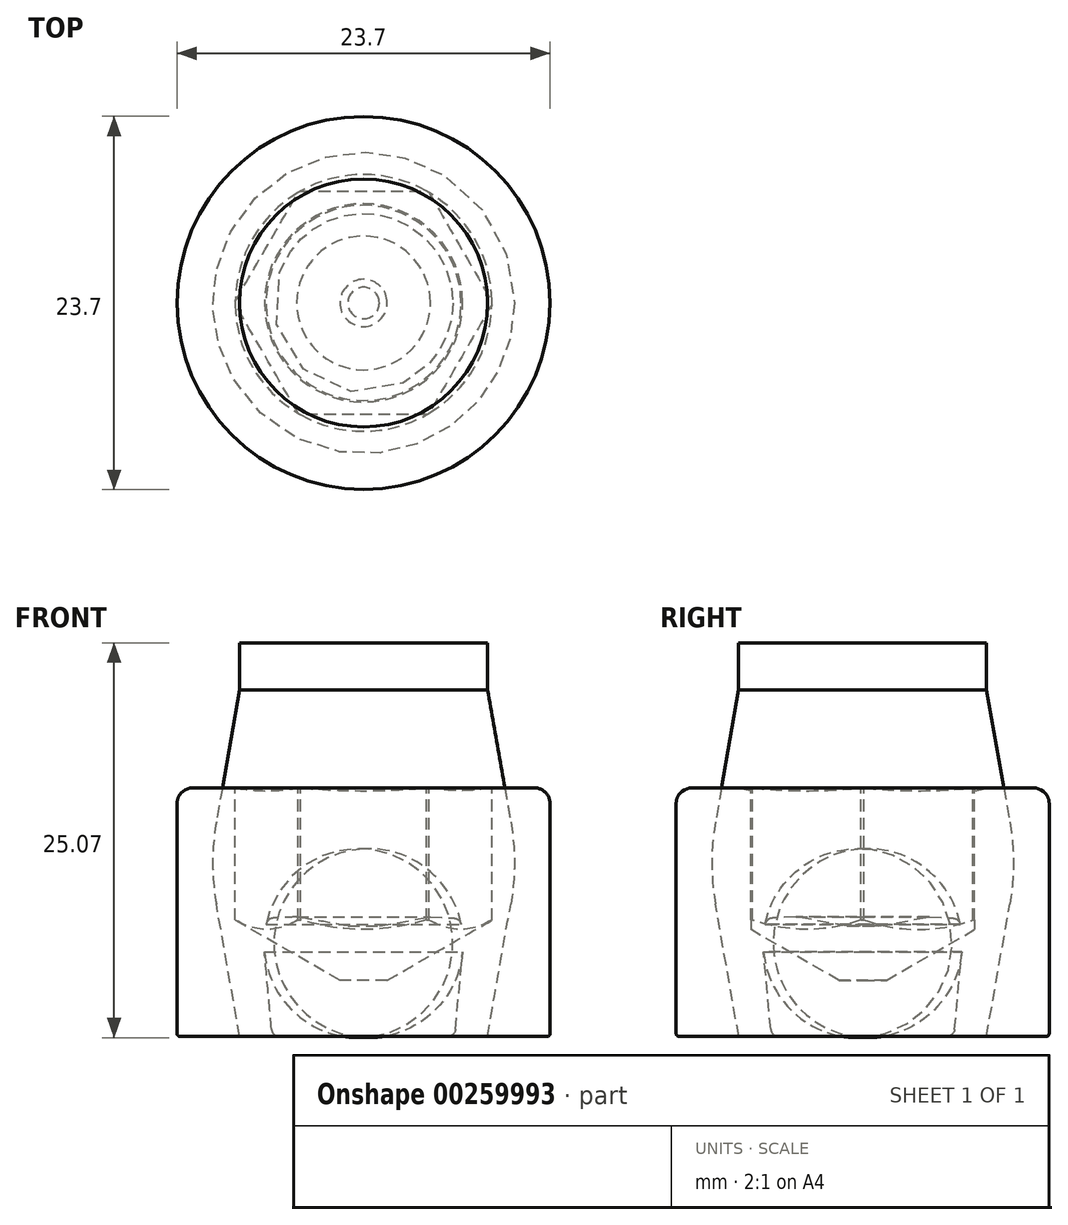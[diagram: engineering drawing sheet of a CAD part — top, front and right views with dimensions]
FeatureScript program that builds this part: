
annotation { "Feature Type Name" : "Feature", "Feature Type Description" : "" }
export const myFeature = defineFeature(function(context is Context, id is Id, definition is map)
    precondition{}
    {
        {
            var Q0;
            Q0=qCreatedBy(makeId("Front.planeOp"),FACE);
            var sketch = newSketch(context, id + "F0", { "sketchPlane" : qUnion([Q0])});
            skLineSegment(sketch, "E0", {"start": v(0, 0) * mm, "end": v(0, 3.56) * mm, "construction": true});
            skLineSegment(sketch, "E1", {"start": v(8.15, 15.8) * mm, "end": v(10.84, 15.8) * mm});
            skLineSegment(sketch, "E2", {"start": v(11.84, 14.8) * mm, "end": v(11.85, 0.2) * mm});
            skLineSegment(sketch, "E3", {"start": v(11.65, 0) * mm, "end": v(0, 0) * mm});
            skPoint(sketch, "E4.visualSharp", {"position": v(11.84, 15.8) * mm});
            skArc(sketch, "E4.filletArc", {"start": v(11.84, 14.8) * mm, "mid": v(11.55, 15.5) * mm, "end": v(10.84, 15.8) * mm});
            skPoint(sketch, "E5.visualSharp", {"position": v(11.85, 0) * mm});
            skArc(sketch, "E5.filletArc", {"start": v(11.65, 0) * mm, "mid": v(11.79, 0.06) * mm, "end": v(11.85, 0.2) * mm});
            skLineSegment(sketch, "E6", {"start": v(8.15, 15.8) * mm, "end": v(8.15, 7.4) * mm});
            skLineSegment(sketch, "E7", {"start": v(8.15, 7.4) * mm, "end": v(1.5, 3.56) * mm});
            skLineSegment(sketch, "E8", {"start": v(1.5, 3.56) * mm, "end": v(0, 3.56) * mm});
            skLineSegment(sketch, "E9", {"start": v(0, 3.56) * mm, "end": v(0, 0) * mm});
            skSolve(sketch);
        }
        {
            var Q0;
            Q0=qSketchRegion(id+"F0",true);
            var Q1;
            Q1=sQuery(id+"F0.wireOp",EDGE,"E9");
            revolve(context, id + "F1", {"entities" : qUnion([Q0]), "axis" : qUnion([Q1]), "revolveType" : RevolveType.FULL});
        }
        {
            var Q0;
            Q0=makeQuery(id+"F1.opRevolve","SWEPT_FACE",FACE,{"disambiguationData":[OSD([sQuery(id+"F0.wireOp",EDGE,"E1")])]});
            var sketch = newSketch(context, id + "F2", { "sketchPlane" : qUnion([Q0])});
            skCircle(sketch, "E10", {"center": v(0, 0) * mm, "radius": 10.84 * mm});
            skCircle(sketch, "E11.cCircle", {"center": v(0, 0) * mm, "radius": 7.1 * mm, "construction": true});
            skLineSegment(sketch, "E11.0", {"start": v(-4.1, 7.1) * mm, "end": v(4.1, 7.1) * mm});
            skLineSegment(sketch, "E11.1", {"start": v(4.1, 7.1) * mm, "end": v(8.2, 0) * mm});
            skLineSegment(sketch, "E11.2", {"start": v(8.2, 0) * mm, "end": v(4.1, -7.1) * mm});
            skLineSegment(sketch, "E11.3", {"start": v(4.1, -7.1) * mm, "end": v(-4.1, -7.1) * mm});
            skLineSegment(sketch, "E11.4", {"start": v(-4.1, -7.1) * mm, "end": v(-8.2, 0) * mm});
            skLineSegment(sketch, "E11.5", {"start": v(-8.2, 0) * mm, "end": v(-4.1, 7.1) * mm});
            skPoint(sketch, "E11.0.midPoint", {"position": v(0, 7.1) * mm});
            skSolve(sketch);
        }
        {
            var Q0;
            Q0=qSketchRegion(id+"F2",true);
            var Q1;
            Q1=makeQuery(id+"F1.opRevolve","SWEPT_FACE",FACE,{"disambiguationData":[OSD([sQuery(id+"F0.wireOp",EDGE,"E7")])]});
            extrude(context, id + "F3", {"entities" : qUnion([Q0]), "operationType" : NewBodyOperationType.ADD, "endBound" : BoundingType.UP_TO_SURFACE, "oppositeDirection" : true, "endBoundEntityFace" : qUnion([Q1]), "depth" : 25 * mm});
        }
        {
            var Q0;
            Q0=makeQuery(id+"F3.boolean.opBoolean","MERGE",FACE,{"derivedFrom":[makeQuery(id+"F1.opRevolve","SWEPT_FACE",FACE,{"disambiguationData":[OSD([sQuery(id+"F0.wireOp",EDGE,"E1")])]}),makeQuery(id+"F3.opExtrude","CAP_FACE",FACE,{"disambiguationData":[OSD([sQuery(id+"F2.wireOp",EDGE,"axiUSiGf-8ymJ-Ezfh-tHsk-ULXXzRlxOoBz"),sQuery(id+"F2.wireOp",EDGE,"WrdyBTnM-XU54-uk96-2Sjo-h1HHDxb1zyqn"),sQuery(id+"F2.wireOp",EDGE,"7iNK7enz-fUzD-7EQp-KRCh-aPKnPlRcPdaK"),sQuery(id+"F2.wireOp",EDGE,"e7c95674-c634-4135-8625-61586754ee6a.1.0"),sQuery(id+"F2.wireOp",EDGE,"e7c95674-c634-4135-8625-61586754ee6a.1.1"),sQuery(id+"F2.wireOp",EDGE,"e7c95674-c634-4135-8625-61586754ee6a.1.2"),sQuery(id+"F2.wireOp",EDGE,"e7c95674-c634-4135-8625-61586754ee6a.2.0"),sQuery(id+"F2.wireOp",EDGE,"e7c95674-c634-4135-8625-61586754ee6a.2.1"),sQuery(id+"F2.wireOp",EDGE,"e7c95674-c634-4135-8625-61586754ee6a.2.2"),sQuery(id+"F2.wireOp",EDGE,"e7c95674-c634-4135-8625-61586754ee6a.3.0"),sQuery(id+"F2.wireOp",EDGE,"e7c95674-c634-4135-8625-61586754ee6a.3.1"),sQuery(id+"F2.wireOp",EDGE,"e7c95674-c634-4135-8625-61586754ee6a.3.2"),sQuery(id+"F2.wireOp",EDGE,"e7c95674-c634-4135-8625-61586754ee6a.4.0"),sQuery(id+"F2.wireOp",EDGE,"e7c95674-c634-4135-8625-61586754ee6a.4.1"),sQuery(id+"F2.wireOp",EDGE,"e7c95674-c634-4135-8625-61586754ee6a.4.2"),sQuery(id+"F2.wireOp",EDGE,"e7c95674-c634-4135-8625-61586754ee6a.5.0"),sQuery(id+"F2.wireOp",EDGE,"e7c95674-c634-4135-8625-61586754ee6a.5.1"),sQuery(id+"F2.wireOp",EDGE,"e7c95674-c634-4135-8625-61586754ee6a.5.2"),sQuery(id+"F2.wireOp",EDGE,"c34f7dbc-1fd9-48ae-9599-0fb72b0d65de.filletArc"),sQuery(id+"F2.wireOp",EDGE,"5fecc0f4-c57f-42b8-a97f-f8fbf54cf4db.filletArc"),sQuery(id+"F2.wireOp",EDGE,"b077568f-b672-48a6-a184-fa18c1575088.filletArc"),sQuery(id+"F2.wireOp",EDGE,"4c4ba650-eb3b-40a6-a5b6-7d0bcd232093.filletArc"),sQuery(id+"F2.wireOp",EDGE,"b016cc09-0b8d-437b-9508-1d7630c9d4ff.filletArc"),sQuery(id+"F2.wireOp",EDGE,"d5479cb3-145b-41e2-b586-5ab3f6452500.filletArc"),sQuery(id+"F2.wireOp",EDGE,"E10")])],"isStart":true})]});
            var sketch = newSketch(context, id + "F4", { "sketchPlane" : qUnion([Q0])});
            skCircle(sketch, "E12", {"center": v(0, 0) * mm, "radius": 8.15 * mm});
            skSolve(sketch);
        }
        {
            var Q0;
            Q0=qSketchRegion(id+"F4",true);
            extrude(context, id + "F5", {"entities" : qUnion([Q0]), "operationType" : NewBodyOperationType.REMOVE, "oppositeDirection" : true, "depth" : 1 * mm, "hasDraft" : true, "draftAngle" : 80 * degree, "draftPullDirection" : true});
        }
        {
            var Q0;
            Q0=qCreatedBy(makeId("Front.planeOp"),FACE);
            var sketch = newSketch(context, id + "F6", { "sketchPlane" : qUnion([Q0])});
            skLineSegment(sketch, "E13", {"start": v(0, 0) * mm, "end": v(0, 25) * mm, "construction": true});
            skLineSegment(sketch, "E14", {"start": v(0, 25) * mm, "end": v(7.87, 25) * mm});
            skLineSegment(sketch, "E15", {"start": v(7.87, 25) * mm, "end": v(7.87, 22) * mm});
            skLineSegment(sketch, "E16", {"start": v(7.87, 22) * mm, "end": v(9.35, 13.63) * mm});
            skLineSegment(sketch, "E17", {"start": v(7.86, 0) * mm, "end": v(0, 0) * mm});
            skLineSegment(sketch, "E18", {"start": v(0, 25) * mm, "end": v(0, 0) * mm});
            skLineSegment(sketch, "E19", {"start": v(7.87, 0) * mm, "end": v(9.35, 8.42) * mm});
            skArc(sketch, "E20.filletArc", {"start": v(9.35, 8.42) * mm, "mid": v(9.58, 11.03) * mm, "end": v(9.35, 13.63) * mm});
            skSolve(sketch);
        }
        {
            var Q0;
            Q0=qSketchRegion(id+"F6",true);
            var Q1;
            Q1=sQuery(id+"F6.wireOp",EDGE,"E18");
            revolve(context, id + "F7", {"entities" : qUnion([Q0]), "axis" : qUnion([Q1]), "revolveType" : RevolveType.FULL});
        }
        {
            var Q0;
            Q0=qCreatedBy(makeId("Front.planeOp"),FACE);
            var sketch = newSketch(context, id + "F8", { "sketchPlane" : qUnion([Q0])});
            skLineSegment(sketch, "E21", {"start": v(0, 0) * mm, "end": v(0, 7.03) * mm});
            skLineSegment(sketch, "E22", {"start": v(6.3, 5.39) * mm, "end": v(5.84, 0.45) * mm});
            skLineSegment(sketch, "E23", {"start": v(5.34, 0) * mm, "end": v(0, 0) * mm});
            skPoint(sketch, "E24.visualSharp", {"position": v(5.8, 0) * mm});
            skArc(sketch, "E24.filletArc", {"start": v(5.34, 0) * mm, "mid": v(5.68, 0.13) * mm, "end": v(5.84, 0.45) * mm});
            skLineSegment(sketch, "E25", {"start": v(0, 7.03) * mm, "end": v(0, 0) * mm, "construction": true});
            skLineSegment(sketch, "E26", {"start": v(0, 7.03) * mm, "end": v(1, 7.03) * mm});
            skLineSegment(sketch, "E27", {"start": v(1, 7.03) * mm, "end": v(4.25, 7.6) * mm});
            skLineSegment(sketch, "E28", {"start": v(4.25, 7.6) * mm, "end": v(5.74, 7.52) * mm});
            skArc(sketch, "E29.filletArc", {"start": v(6.3, 5.39) * mm, "mid": v(6.31, 6.26) * mm, "end": v(6.2, 7.12) * mm});
            skPoint(sketch, "E30.visualSharp", {"position": v(6.11, 7.5) * mm});
            skArc(sketch, "E30.filletArc", {"start": v(6.2, 7.12) * mm, "mid": v(6.04, 7.4) * mm, "end": v(5.74, 7.52) * mm});
            skLineSegment(sketch, "E31", {"start": v(6.3, 5.39) * mm, "end": v(6.35, 6) * mm, "construction": true});
            skSolve(sketch);
        }
        {
            var Q0;
            Q0=qSketchRegion(id+"F8",true);
            var Q1;
            Q1=sQuery(id+"F8.wireOp",EDGE,"E21");
            revolve(context, id + "F9", {"entities" : qUnion([Q0]), "axis" : qUnion([Q1]), "revolveType" : RevolveType.FULL});
        }
    });
